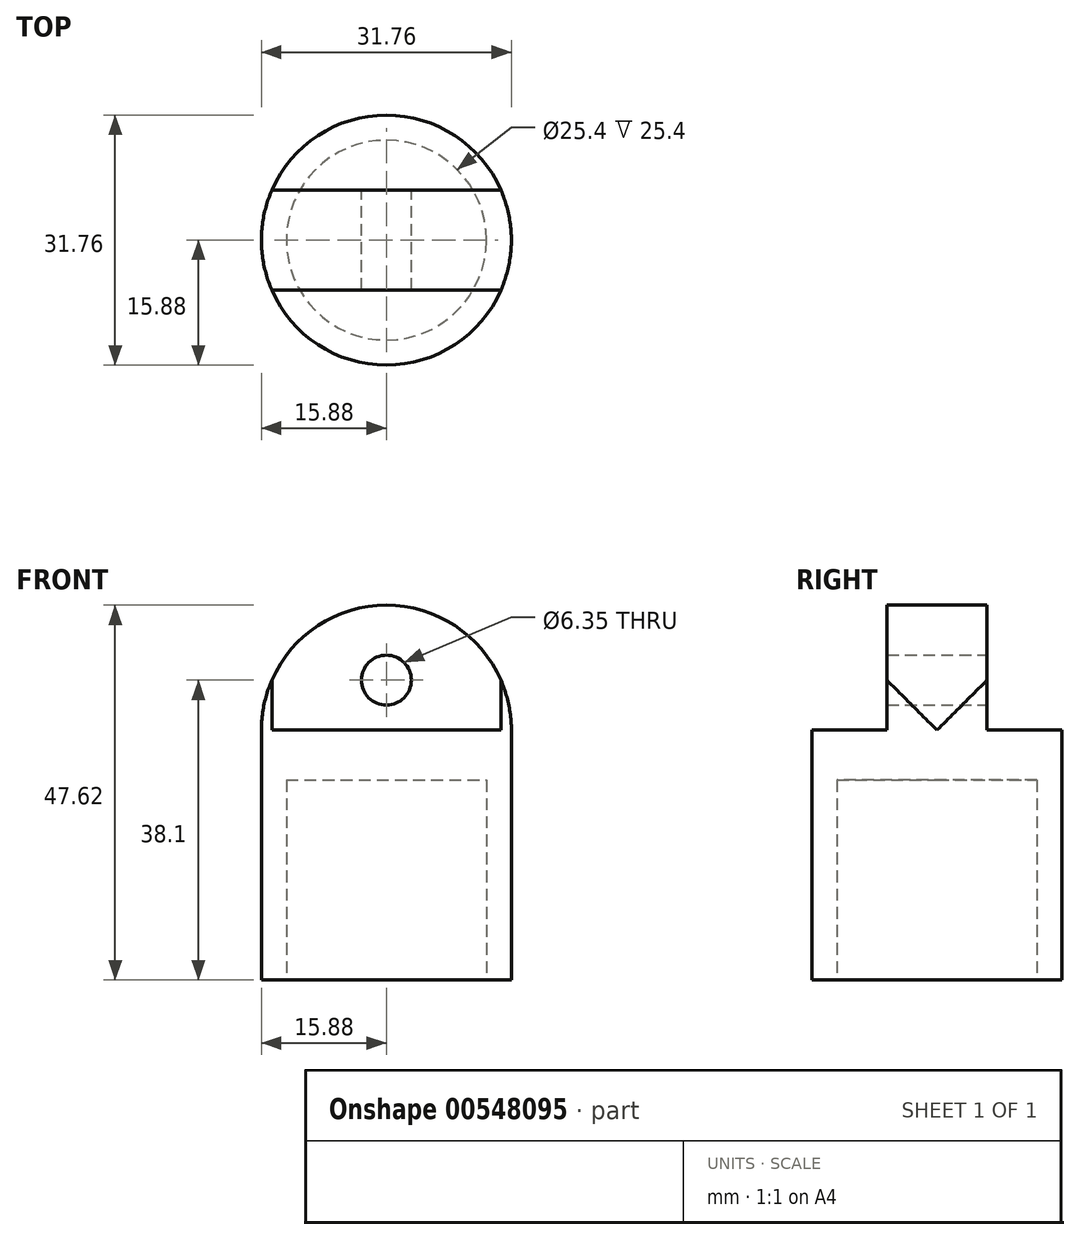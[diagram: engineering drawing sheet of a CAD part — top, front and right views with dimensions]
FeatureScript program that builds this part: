
annotation { "Feature Type Name" : "Feature", "Feature Type Description" : "" }
export const myFeature = defineFeature(function(context is Context, id is Id, definition is map)
    precondition{}
    {
        {
            var Q0;
            Q0=qCreatedBy(makeId("Top.planeOp"),FACE);
            var sketch = newSketch(context, id + "F0", { "sketchPlane" : qUnion([Q0])});
            skCircle(sketch, "E0", {"center": v(0, 0) * mm, "radius": 15.88 * mm});
            skSolve(sketch);
        }
        {
            var Q0;
            Q0=makeQuery(id+"F0.imprint","IMPRINT",FACE,{"disambiguationData":[TD([[makeQuery(id+"F0.imprint","IMPRINT",EDGE,{"derivedFrom":sQuery(id+"F0.wireOp",EDGE,"E0")}),1.0]])]});
            extrude(context, id + "F1", {"entities" : qUnion([Q0]), "depth" : 31.75 * mm, "offsetDistance" : 25.4 * mm});
        }
        {
            var Q0;
            Q0=makeQuery(id+"F1.opExtrude","CAP_FACE",FACE,{"disambiguationData":[OSD([sQuery(id+"F0.wireOp",EDGE,"E0")])],"isStart":true});
            var sketch = newSketch(context, id + "F2", { "sketchPlane" : qUnion([Q0])});
            skCircle(sketch, "E1", {"center": v(0, 0) * mm, "radius": 12.7 * mm});
            skSolve(sketch);
        }
        {
            var Q0;
            Q0=makeQuery(id+"F2.imprint","IMPRINT",FACE,{"disambiguationData":[TD([[makeQuery(id+"F2.imprint","IMPRINT",EDGE,{"derivedFrom":sQuery(id+"F2.wireOp",EDGE,"E1")}),1.0]])]});
            extrude(context, id + "F3", {"entities" : qUnion([Q0]), "operationType" : NewBodyOperationType.REMOVE, "oppositeDirection" : true, "depth" : 25.4 * mm, "offsetDistance" : 25.4 * mm});
        }
        {
            var Q0;
            Q0=qCreatedBy(makeId("Front.planeOp"),FACE);
            var sketch = newSketch(context, id + "F4", { "sketchPlane" : qUnion([Q0])});
            skLineSegment(sketch, "E2.bottom", {"start": v(-15.88, 31.75) * mm, "end": v(15.88, 31.75) * mm});
            skLineSegment(sketch, "E2.top", {"start": v(-15.88, 25.4) * mm, "end": v(15.88, 25.4) * mm});
            skLineSegment(sketch, "E2.left", {"start": v(-15.88, 31.75) * mm, "end": v(-15.88, 25.4) * mm});
            skLineSegment(sketch, "E2.right", {"start": v(15.88, 31.75) * mm, "end": v(15.88, 25.4) * mm});
            skArc(sketch, "E3", {"start": v(15.88, 31.75) * mm, "mid": v(0, 47.62) * mm, "end": v(-15.88, 31.75) * mm});
            skCircle(sketch, "E4", {"center": v(0, 38.1) * mm, "radius": 3.18 * mm});
            skSolve(sketch);
        }
        {
            var Q0;
            Q0=makeQuery(id+"F4.imprint","IMPRINT",FACE,{"disambiguationData":[TD([[makeQuery(id+"F4.imprint","IMPRINT",EDGE,{"derivedFrom":sQuery(id+"F4.wireOp",EDGE,"E2.bottom")}),1.0]])]});
            extrude(context, id + "F5", {"entities" : qUnion([Q0]), "operationType" : NewBodyOperationType.ADD, "depth" : 6.35 * mm, "offsetDistance" : 25.4 * mm, "hasSecondDirection" : true, "secondDirectionOppositeDirection" : true, "secondDirectionDepth" : 6.35 * mm});
        }
        {
            var Q0;
            Q0=qCreatedBy(makeId("Front.planeOp"),FACE);
            var sketch = newSketch(context, id + "F6", { "sketchPlane" : qUnion([Q0])});
            skLineSegment(sketch, "E5.bottom", {"start": v(-15.88, 0) * mm, "end": v(-27.02, 0) * mm});
            skLineSegment(sketch, "E5.top", {"start": v(-15.88, 50.8) * mm, "end": v(-27.02, 50.8) * mm});
            skLineSegment(sketch, "E5.left", {"start": v(-15.88, 0) * mm, "end": v(-15.88, 50.8) * mm});
            skLineSegment(sketch, "E5.right", {"start": v(-27.02, 0) * mm, "end": v(-27.02, 50.8) * mm});
            skLineSegment(sketch, "E6", {"start": v(0, -41.66) * mm, "end": v(0, 66.8) * mm});
            skSolve(sketch);
        }
        {
            var Q0;
            Q0=makeQuery(id+"F6.imprint","IMPRINT",FACE,{"disambiguationData":[TD([[makeQuery(id+"F6.imprint","IMPRINT",EDGE,{"derivedFrom":sQuery(id+"F6.wireOp",EDGE,"E5.bottom")}),-1.0]])]});
            var Q1;
            Q1=sQuery(id+"F6.wireOp",EDGE,"E6");
            revolve(context, id + "F7", {"operationType" : NewBodyOperationType.REMOVE, "entities" : qUnion([Q0]), "axis" : qUnion([Q1]), "revolveType" : RevolveType.FULL, "oppositeDirection" : true});
        }
    });
